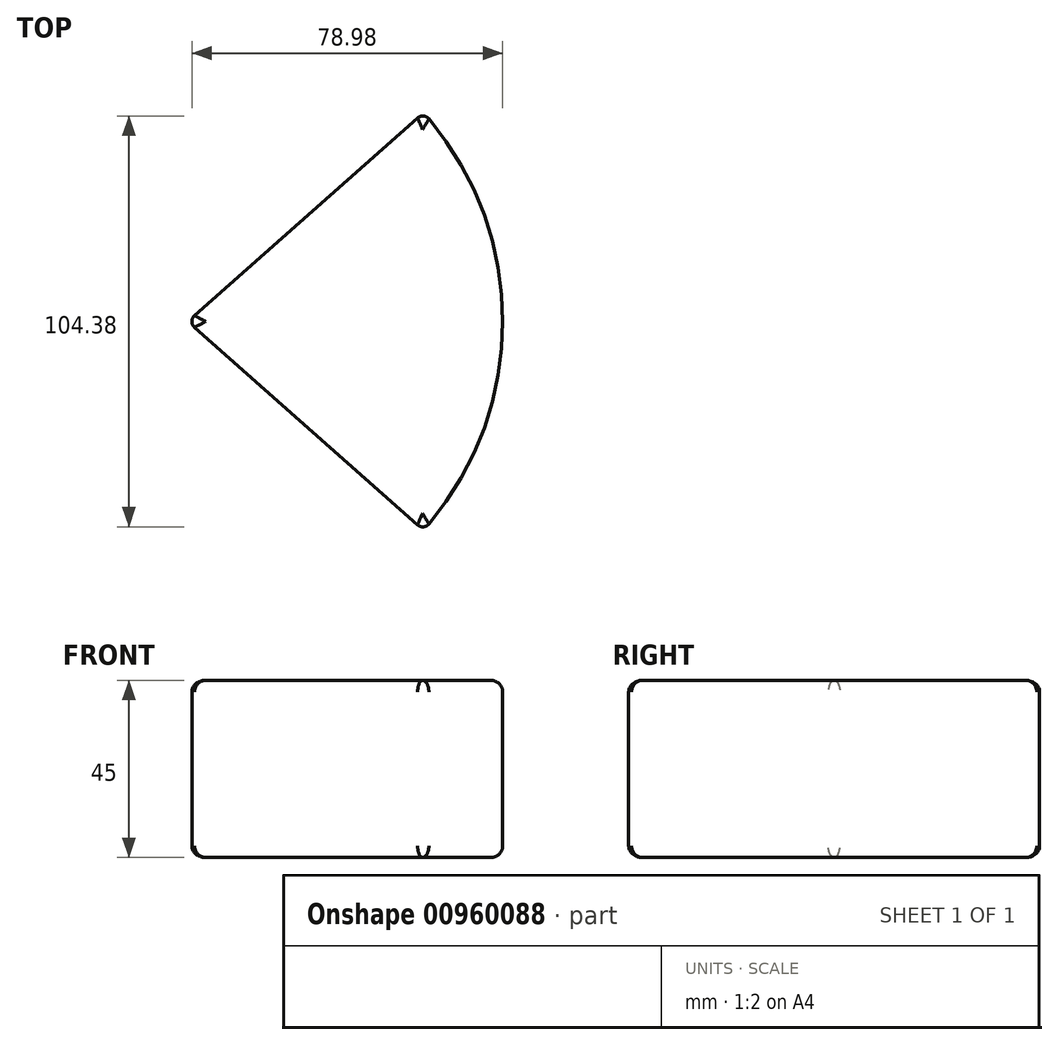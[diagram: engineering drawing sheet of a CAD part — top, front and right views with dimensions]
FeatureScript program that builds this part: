
annotation { "Feature Type Name" : "Feature", "Feature Type Description" : "" }
export const myFeature = defineFeature(function(context is Context, id is Id, definition is map)
    precondition{}
    {
        {
            var Q0;
            Q0=qCreatedBy(makeId("Top.planeOp"),FACE);
            var sketch = newSketch(context, id + "F0", { "sketchPlane" : qUnion([Q0])});
            skLineSegment(sketch, "E0", {"start": v(0, 0) * mm, "end": v(59.9, 53.03) * mm});
            skArc(sketch, "E1", {"start": v(59.9, 53.03) * mm, "mid": v(80, 0) * mm, "end": v(59.9, -53.03) * mm});
            skLineSegment(sketch, "E2", {"start": v(59.9, -53.03) * mm, "end": v(0, 0) * mm});
            skSolve(sketch);
        }
        {
            var Q0;
            Q0=makeQuery(id+"F0.imprint","IMPRINT",FACE,{"disambiguationData":[TD([[makeQuery(id+"F0.imprint","IMPRINT",EDGE,{"derivedFrom":sQuery(id+"F0.wireOp",EDGE,"E0")}),-1.0]])]});
            extrude(context, id + "F1", {"entities" : qUnion([Q0]), "depth" : 45 * mm, "offsetDistance" : 25 * mm});
        }
        {
            var Q0;
            Q0=makeQuery(id+"F1.opExtrude","SWEPT_EDGE",EDGE,{"disambiguationData":[OSD([sQuery(id+"F0.wireOp",EDGE,"E0"),sQuery(id+"F0.wireOp",EDGE,"E2")])]});
            var Q1;
            Q1=makeQuery(id+"F1.opExtrude","SWEPT_EDGE",EDGE,{"disambiguationData":[OSD([sQuery(id+"F0.wireOp",EDGE,"E1"),sQuery(id+"F0.wireOp",EDGE,"E2")])]});
            var Q2;
            Q2=makeQuery(id+"F1.opExtrude","SWEPT_EDGE",EDGE,{"disambiguationData":[OSD([sQuery(id+"F0.wireOp",EDGE,"E0"),sQuery(id+"F0.wireOp",EDGE,"E1")])]});
            fillet(context, id + "F2", {"entities" : qUnion([Q0, Q1, Q2]), "radius" : 2 * mm, "tangentPropagation" : true, "allowEdgeOverflow" : false});
        }
        {
            var Q0;
            Q0=makeQuery(id+"F1.opExtrude","CAP_EDGE",EDGE,{"disambiguationData":[OSD([sQuery(id+"F0.wireOp",EDGE,"E1")])],"isStart":false});
            var Q1;
            Q1=makeQuery(id+"F1.opExtrude","CAP_EDGE",EDGE,{"disambiguationData":[OSD([sQuery(id+"F0.wireOp",EDGE,"E1")])],"isStart":true});
            fillet(context, id + "F3", {"entities" : qUnion([Q0, Q1]), "radius" : 3 * mm, "tangentPropagation" : true, "allowEdgeOverflow" : false});
        }
    });
